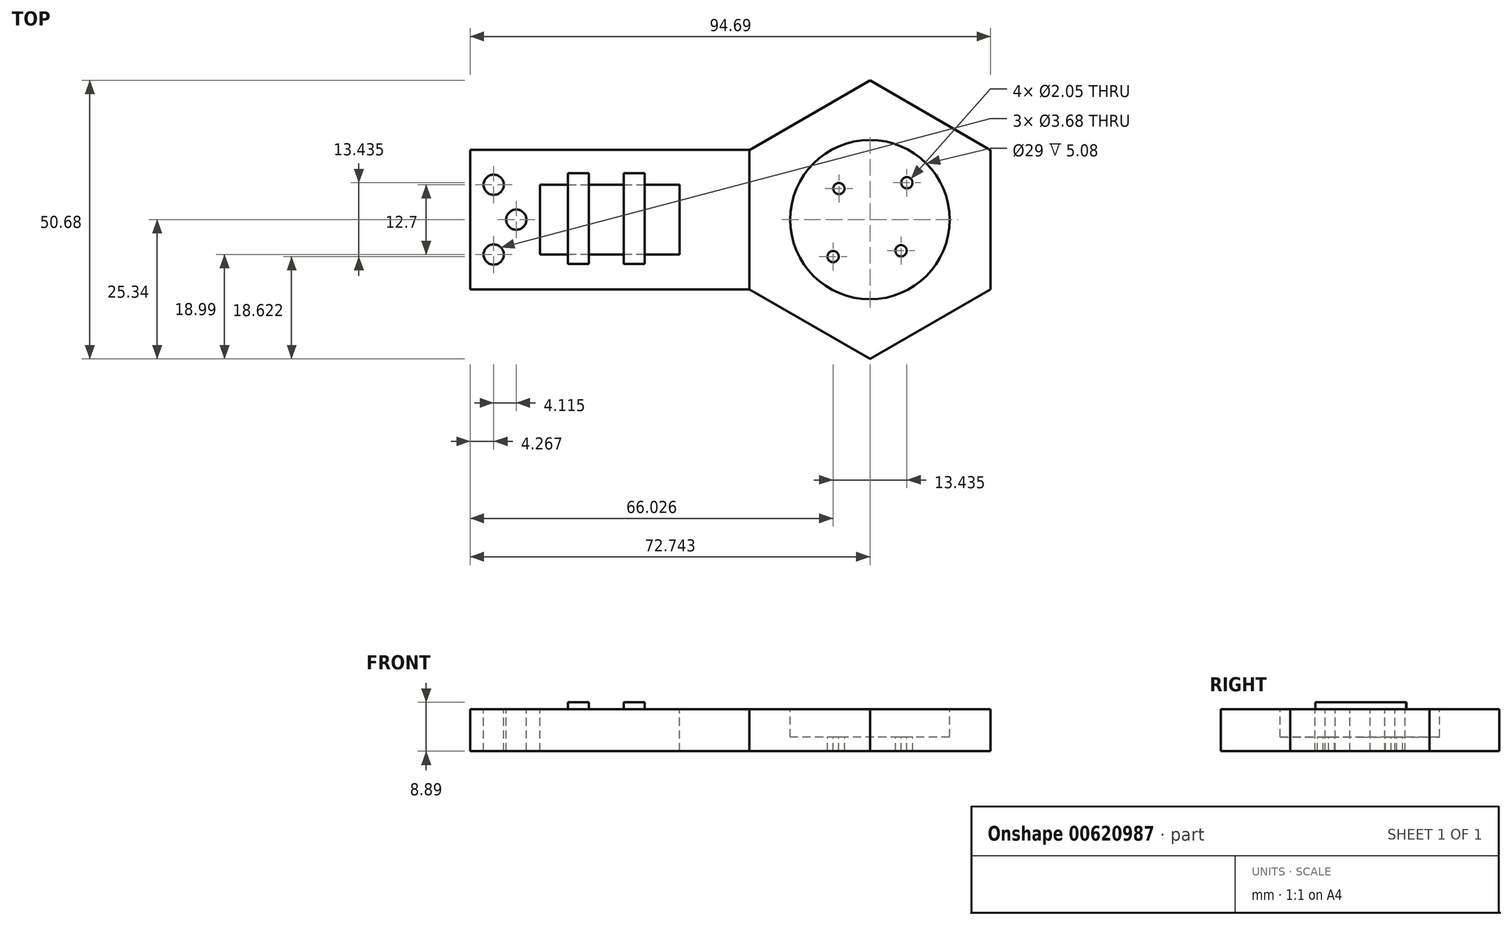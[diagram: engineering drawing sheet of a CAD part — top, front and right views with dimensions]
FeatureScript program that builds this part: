
annotation { "Feature Type Name" : "Feature", "Feature Type Description" : "" }
export const myFeature = defineFeature(function(context is Context, id is Id, definition is map)
    precondition{}
    {
        {
            var Q0;
            Q0=qCreatedBy(makeId("Top.planeOp"),FACE);
            var sketch = newSketch(context, id + "F0", { "sketchPlane" : qUnion([Q0])});
            skLineSegment(sketch, "E0.bottom", {"start": v(50.8, -12.7) * mm, "end": v(0, -12.7) * mm});
            skLineSegment(sketch, "E0.top", {"start": v(50.8, 12.7) * mm, "end": v(0, 12.7) * mm});
            skLineSegment(sketch, "E0.left", {"start": v(50.8, -12.7) * mm, "end": v(50.8, 12.7) * mm});
            skPoint(sketch, "E0.middle", {"position": v(0, 0) * mm});
            skLineSegment(sketch, "E1", {"start": v(0, 12.7) * mm, "end": v(0, -12.7) * mm});
            skPoint(sketch, "E2.orphan", {"position": v(-50.8, 12.7) * mm});
            skPoint(sketch, "E3.orphan", {"position": v(-50.8, -12.7) * mm});
            skSolve(sketch);
        }
        {
            var Q0;
            Q0=makeQuery(id+"F0.imprint","IMPRINT",FACE,{"disambiguationData":[TD([[makeQuery(id+"F0.imprint","IMPRINT",EDGE,{"derivedFrom":sQuery(id+"F0.wireOp",EDGE,"E0.bottom")}),-1.0]])]});
            extrude(context, id + "F1", {"entities" : qUnion([Q0]), "depth" : 7.62 * mm, "offsetDistance" : 25.4 * mm});
        }
        {
            var Q0;
            Q0=qCreatedBy(makeId("Top.planeOp"),FACE);
            var sketch = newSketch(context, id + "F2", { "sketchPlane" : qUnion([Q0])});
            skCircle(sketch, "E4.cCircle", {"center": v(72.74, 0) * mm, "radius": 21.95 * mm, "construction": true});
            skLineSegment(sketch, "E4.0", {"start": v(94.7, 12.67) * mm, "end": v(94.7, -12.67) * mm});
            skLineSegment(sketch, "E4.1", {"start": v(94.7, -12.67) * mm, "end": v(72.74, -25.34) * mm});
            skLineSegment(sketch, "E4.2", {"start": v(72.74, -25.34) * mm, "end": v(50.8, -12.67) * mm});
            skLineSegment(sketch, "E4.3", {"start": v(50.8, -12.67) * mm, "end": v(50.8, 12.67) * mm});
            skLineSegment(sketch, "E4.4", {"start": v(50.8, 12.67) * mm, "end": v(72.74, 25.34) * mm});
            skLineSegment(sketch, "E4.5", {"start": v(72.74, 25.34) * mm, "end": v(94.7, 12.67) * mm});
            skPoint(sketch, "E4.0.midPoint", {"position": v(94.7, 0) * mm});
            skSolve(sketch);
        }
        {
            var Q0;
            Q0=makeQuery(id+"F2.imprint","IMPRINT",FACE,{"disambiguationData":[TD([[makeQuery(id+"F2.imprint","IMPRINT",EDGE,{"derivedFrom":sQuery(id+"F2.wireOp",EDGE,"E4.0")}),-1.0]])]});
            extrude(context, id + "F3", {"entities" : qUnion([Q0]), "depth" : 7.62 * mm, "offsetDistance" : 25.4 * mm});
        }
        {
            var Q0;
            Q0=makeQuery(id+"F1.opExtrude","CAP_FACE",FACE,{"disambiguationData":[OSD([sQuery(id+"F0.wireOp",EDGE,"E0.bottom"),sQuery(id+"F0.wireOp",EDGE,"E0.top"),sQuery(id+"F0.wireOp",EDGE,"E0.left"),sQuery(id+"F0.wireOp",EDGE,"E0.right")])],"isStart":false});
            var sketch = newSketch(context, id + "F4", { "sketchPlane" : qUnion([Q0])});
            skLineSegment(sketch, "E5", {"start": v(12.7, 6.35) * mm, "end": v(38.1, 6.35) * mm});
            skLineSegment(sketch, "E6", {"start": v(38.1, 6.35) * mm, "end": v(38.1, -6.35) * mm});
            skLineSegment(sketch, "E7", {"start": v(38.1, -6.35) * mm, "end": v(12.7, -6.35) * mm});
            skLineSegment(sketch, "E8", {"start": v(12.7, -6.35) * mm, "end": v(12.7, 6.35) * mm});
            skSolve(sketch);
        }
        {
            var Q0;
            Q0=makeQuery(id+"F4.imprint","IMPRINT",FACE,{"disambiguationData":[TD([[makeQuery(id+"F4.imprint","IMPRINT",EDGE,{"derivedFrom":sQuery(id+"F4.wireOp",EDGE,"E5")}),-1.0]])]});
            extrude(context, id + "F5", {"entities" : qUnion([Q0]), "operationType" : NewBodyOperationType.REMOVE, "endBound" : BoundingType.THROUGH_ALL, "oppositeDirection" : true, "depth" : 25.4 * mm, "offsetDistance" : 25.4 * mm});
        }
        {
            var Q0;
            Q0=makeQuery(id+"F3.opExtrude","CAP_FACE",FACE,{"disambiguationData":[OSD([sQuery(id+"F2.wireOp",EDGE,"E4.0"),sQuery(id+"F2.wireOp",EDGE,"E4.1"),sQuery(id+"F2.wireOp",EDGE,"E4.2"),sQuery(id+"F2.wireOp",EDGE,"E4.3"),sQuery(id+"F2.wireOp",EDGE,"E4.4"),sQuery(id+"F2.wireOp",EDGE,"E4.5")])],"isStart":false});
            var sketch = newSketch(context, id + "F6", { "sketchPlane" : qUnion([Q0])});
            skCircle(sketch, "E9", {"center": v(72.74, 0) * mm, "radius": 14.5 * mm});
            skSolve(sketch);
        }
        {
            var Q0;
            Q0=qSketchRegion(id+"F6",true);
            extrude(context, id + "F7", {"entities" : qUnion([Q0]), "operationType" : NewBodyOperationType.REMOVE, "oppositeDirection" : true, "depth" : 5.08 * mm, "offsetDistance" : 25.4 * mm});
        }
        {
            var Q0;
            Q0=makeQuery(id+"F7.boolean.opBoolean","COPY",FACE,{"derivedFrom":makeQuery(id+"F7.opExtrude","CAP_FACE",FACE,{"disambiguationData":[OSD([sQuery(id+"F6.wireOp",EDGE,"E9")])],"isStart":false})});
            var sketch = newSketch(context, id + "F8", { "sketchPlane" : qUnion([Q0])});
            skLineSegment(sketch, "E10", {"start": v(72.74, 0) * mm, "end": v(79.46, 6.72) * mm});
            skSolve(sketch);
        }
        {
            var Q0;
            Q0=makeQuery(id+"F8.imprint","IMPRINT",FACE,{"disambiguationData":[TD([[makeQuery(id+"F8.imprint","IMPRINT",EDGE,{"derivedFrom":makeQuery(id+"F7.boolean.opBoolean","COPY",EDGE,{"derivedFrom":makeQuery(id+"F7.opExtrude","CAP_EDGE",EDGE,{"disambiguationData":[OSD([sQuery(id+"F6.wireOp",EDGE,"E9")])],"isStart":false})})}),1.0]])]});
            var sketch = newSketch(context, id + "F9", { "sketchPlane" : qUnion([Q0])});
            skCircle(sketch, "E11", {"center": v(67.09, 5.66) * mm, "radius": 1.02 * mm});
            skSolve(sketch);
        }
        {
            var Q0;
            Q0=makeQuery(id+"F8.imprint","IMPRINT",FACE,{"disambiguationData":[TD([[makeQuery(id+"F8.imprint","IMPRINT",EDGE,{"derivedFrom":makeQuery(id+"F7.boolean.opBoolean","COPY",EDGE,{"derivedFrom":makeQuery(id+"F7.opExtrude","CAP_EDGE",EDGE,{"disambiguationData":[OSD([sQuery(id+"F6.wireOp",EDGE,"E9")])],"isStart":false})})}),1.0]])]});
            var sketch = newSketch(context, id + "F10", { "sketchPlane" : qUnion([Q0])});
            skCircle(sketch, "E12", {"center": v(79.46, 6.72) * mm, "radius": 1.02 * mm});
            skSolve(sketch);
        }
        {
            var Q0;
            Q0=makeQuery(id+"F8.imprint","IMPRINT",FACE,{"disambiguationData":[TD([[makeQuery(id+"F8.imprint","IMPRINT",EDGE,{"derivedFrom":makeQuery(id+"F7.boolean.opBoolean","COPY",EDGE,{"derivedFrom":makeQuery(id+"F7.opExtrude","CAP_EDGE",EDGE,{"disambiguationData":[OSD([sQuery(id+"F6.wireOp",EDGE,"E9")])],"isStart":false})})}),1.0]])]});
            var sketch = newSketch(context, id + "F11", { "sketchPlane" : qUnion([Q0])});
            skCircle(sketch, "E13", {"center": v(78.4, -5.66) * mm, "radius": 1.02 * mm});
            skSolve(sketch);
        }
        {
            var Q0;
            Q0=makeQuery(id+"F8.imprint","IMPRINT",FACE,{"disambiguationData":[TD([[makeQuery(id+"F8.imprint","IMPRINT",EDGE,{"derivedFrom":makeQuery(id+"F7.boolean.opBoolean","COPY",EDGE,{"derivedFrom":makeQuery(id+"F7.opExtrude","CAP_EDGE",EDGE,{"disambiguationData":[OSD([sQuery(id+"F6.wireOp",EDGE,"E9")])],"isStart":false})})}),1.0]])]});
            var sketch = newSketch(context, id + "F12", { "sketchPlane" : qUnion([Q0])});
            skCircle(sketch, "E14", {"center": v(66.03, -6.72) * mm, "radius": 1.02 * mm});
            skSolve(sketch);
        }
        {
            var Q0;
            Q0=qSketchRegion(id+"F9",true);
            extrude(context, id + "F13", {"entities" : qUnion([Q0]), "operationType" : NewBodyOperationType.REMOVE, "endBound" : BoundingType.THROUGH_ALL, "oppositeDirection" : true, "depth" : 25.4 * mm, "offsetDistance" : 25.4 * mm});
        }
        {
            var Q0;
            Q0=qSketchRegion(id+"F10",true);
            extrude(context, id + "F14", {"entities" : qUnion([Q0]), "operationType" : NewBodyOperationType.REMOVE, "endBound" : BoundingType.THROUGH_ALL, "oppositeDirection" : true, "depth" : 25.4 * mm, "offsetDistance" : 25.4 * mm});
        }
        {
            var Q0;
            Q0=qSketchRegion(id+"F11",true);
            extrude(context, id + "F15", {"entities" : qUnion([Q0]), "operationType" : NewBodyOperationType.REMOVE, "endBound" : BoundingType.THROUGH_ALL, "oppositeDirection" : true, "depth" : 25.4 * mm, "offsetDistance" : 25.4 * mm});
        }
        {
            var Q0;
            Q0=qSketchRegion(id+"F12",true);
            extrude(context, id + "F16", {"entities" : qUnion([Q0]), "operationType" : NewBodyOperationType.REMOVE, "endBound" : BoundingType.THROUGH_ALL, "oppositeDirection" : true, "depth" : 25.4 * mm, "offsetDistance" : 25.4 * mm});
        }
        {
            var Q0;
            Q0=makeQuery(id+"F1.opExtrude","CAP_FACE",FACE,{"disambiguationData":[OSD([sQuery(id+"F0.wireOp",EDGE,"E0.bottom"),sQuery(id+"F0.wireOp",EDGE,"E0.top"),sQuery(id+"F0.wireOp",EDGE,"E0.left"),sQuery(id+"F0.wireOp",EDGE,"E0.right")])],"isStart":false});
            var sketch = newSketch(context, id + "F17", { "sketchPlane" : qUnion([Q0])});
            skLineSegment(sketch, "E15.bottom", {"start": v(17.78, -8.04) * mm, "end": v(21.59, -8.04) * mm});
            skLineSegment(sketch, "E15.top", {"start": v(17.78, 8.47) * mm, "end": v(21.59, 8.47) * mm});
            skLineSegment(sketch, "E15.left", {"start": v(17.78, -8.04) * mm, "end": v(17.78, 8.47) * mm});
            skLineSegment(sketch, "E15.right", {"start": v(21.59, -8.04) * mm, "end": v(21.59, 8.47) * mm});
            skLineSegment(sketch, "E16.bottom", {"start": v(27.94, -8.08) * mm, "end": v(31.75, -8.08) * mm});
            skLineSegment(sketch, "E16.top", {"start": v(27.94, 8.43) * mm, "end": v(31.75, 8.43) * mm});
            skLineSegment(sketch, "E16.left", {"start": v(27.94, -8.08) * mm, "end": v(27.94, 8.43) * mm});
            skLineSegment(sketch, "E16.right", {"start": v(31.75, -8.08) * mm, "end": v(31.75, 8.43) * mm});
            skSolve(sketch);
        }
        {
            var Q0;
            Q0=qSketchRegion(id+"F17",true);
            extrude(context, id + "F18", {"entities" : qUnion([Q0]), "operationType" : NewBodyOperationType.ADD, "depth" : 1.27 * mm, "offsetDistance" : 25.4 * mm});
        }
        {
            var Q0;
            Q0=makeQuery(id+"F1.opExtrude","CAP_FACE",FACE,{"disambiguationData":[OSD([sQuery(id+"F0.wireOp",EDGE,"E0.bottom"),sQuery(id+"F0.wireOp",EDGE,"E0.top"),sQuery(id+"F0.wireOp",EDGE,"E0.left"),sQuery(id+"F0.wireOp",EDGE,"E0.right")])],"isStart":false});
            var sketch = newSketch(context, id + "F19", { "sketchPlane" : qUnion([Q0])});
            skCircle(sketch, "E17", {"center": v(4.27, 6.35) * mm, "radius": 1.84 * mm});
            skCircle(sketch, "E18", {"center": v(4.27, -6.35) * mm, "radius": 1.84 * mm});
            skCircle(sketch, "E19", {"center": v(8.38, 0) * mm, "radius": 1.84 * mm});
            skSolve(sketch);
        }
        {
            var Q0;
            Q0=qSketchRegion(id+"F19",true);
            extrude(context, id + "F20", {"entities" : qUnion([Q0]), "operationType" : NewBodyOperationType.REMOVE, "endBound" : BoundingType.THROUGH_ALL, "oppositeDirection" : true, "depth" : 25.4 * mm, "offsetDistance" : 25.4 * mm});
        }
    });
